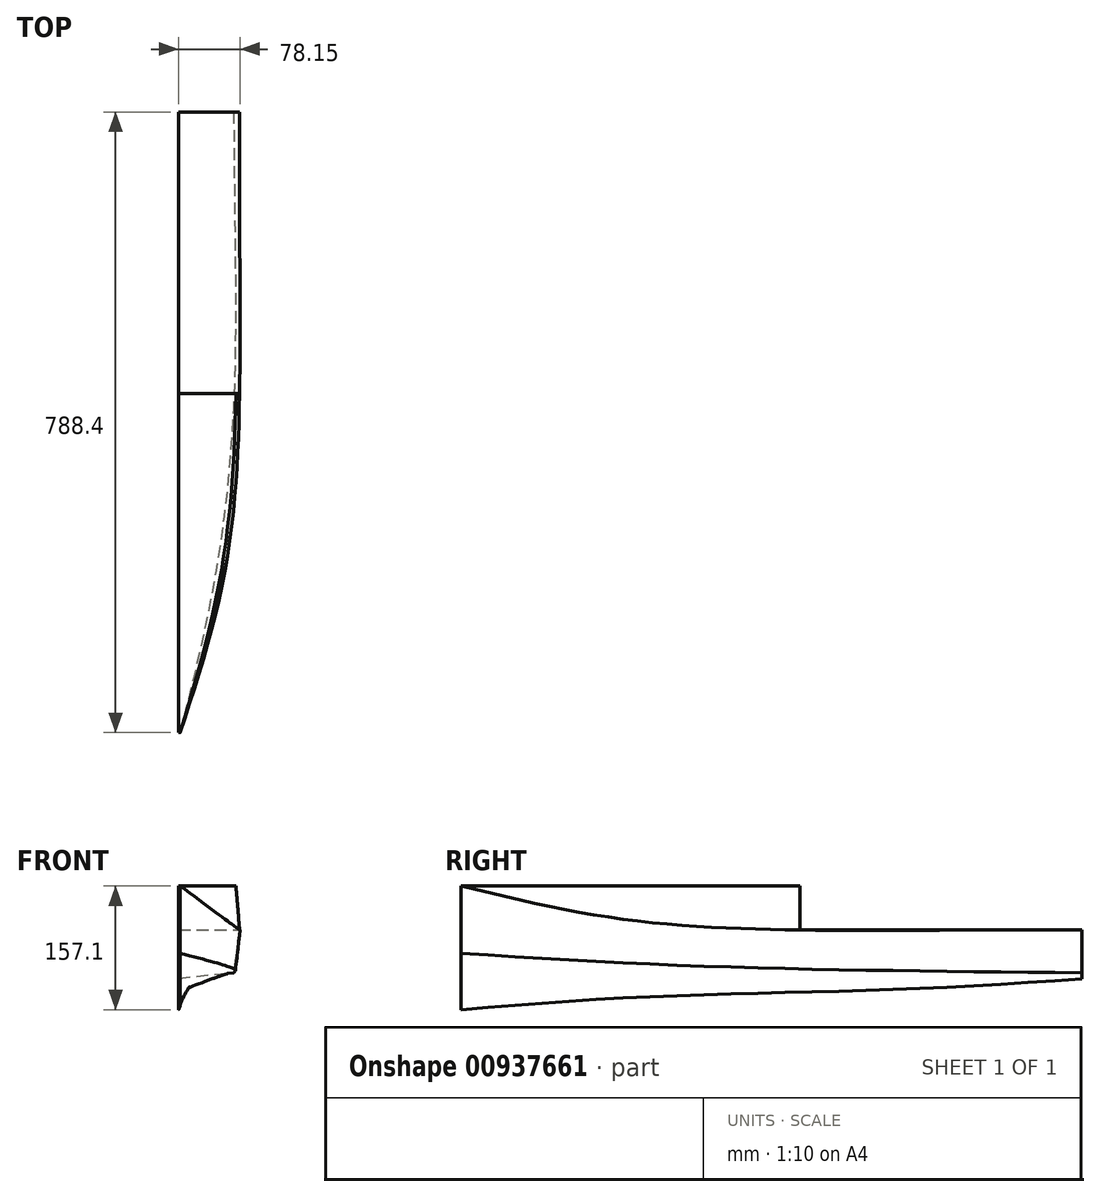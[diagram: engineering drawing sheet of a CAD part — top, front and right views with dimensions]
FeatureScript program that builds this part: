
annotation { "Feature Type Name" : "Feature", "Feature Type Description" : "" }
export const myFeature = defineFeature(function(context is Context, id is Id, definition is map)
    precondition{}
    {
        {
            var Q0;
            Q0=qCreatedBy(makeId("Front.planeOp"),FACE);
            var sketch = newSketch(context, id + "F0", { "sketchPlane" : qUnion([Q0])});
            skLineSegment(sketch, "E0", {"start": v(0, 0) * mm, "end": v(0, 43.5) * mm});
            skLineSegment(sketch, "E1", {"start": v(77.5, 43.5) * mm, "end": v(70, -11) * mm});
            skLineSegment(sketch, "E2", {"start": v(70, -11) * mm, "end": v(0, -18.5) * mm});
            skLineSegment(sketch, "E3", {"start": v(0, -18.5) * mm, "end": v(0, 0) * mm});
            skLineSegment(sketch, "E4", {"start": v(0, 43.5) * mm, "end": v(0, 99.4) * mm});
            skLineSegment(sketch, "E5", {"start": v(0, 99.4) * mm, "end": v(73, 99.4) * mm});
            skLineSegment(sketch, "E6", {"start": v(77.5, 43.5) * mm, "end": v(73, 99.4) * mm});
            skSolve(sketch);
        }
        {
            var Q0;
            Q0=qCreatedBy(makeId("Front.planeOp"),FACE);
            cPlane(context, id + "F1", {"entities" : qUnion([Q0]), "cplaneType" : CPlaneType.OFFSET, "offset" : 131.4 * mm, "width" : 150 * mm, "height" : 150 * mm});
        }
        {
            var Q0;
            Q0=qCreatedBy(id+"F1.planeOp",FACE);
            var sketch = newSketch(context, id + "F2", { "sketchPlane" : qUnion([Q0])});
            skLineSegment(sketch, "E7", {"start": v(0, 0) * mm, "end": v(0, 43.5) * mm});
            skLineSegment(sketch, "E8", {"start": v(77.5, 43.5) * mm, "end": v(71.3, -9.5) * mm});
            skLineSegment(sketch, "E9", {"start": v(71.3, -9.5) * mm, "end": v(0, -27.2) * mm});
            skLineSegment(sketch, "E10", {"start": v(0, -27.2) * mm, "end": v(0, 0) * mm});
            skLineSegment(sketch, "E11", {"start": v(0, 43.5) * mm, "end": v(0, 99.4) * mm});
            skLineSegment(sketch, "E12", {"start": v(0, 99.4) * mm, "end": v(73, 99.4) * mm});
            skLineSegment(sketch, "E13", {"start": v(77.5, 43.5) * mm, "end": v(73, 99.4) * mm});
            skSolve(sketch);
        }
        {
            var Q0;
            Q0=qCreatedBy(makeId("Front.planeOp"),FACE);
            cPlane(context, id + "F3", {"entities" : qUnion([Q0]), "cplaneType" : CPlaneType.OFFSET, "offset" : 358.1 * mm, "width" : 150 * mm, "height" : 150 * mm});
        }
        {
            var Q0;
            Q0=qCreatedBy(id+"F3.planeOp",FACE);
            var sketch = newSketch(context, id + "F4", { "sketchPlane" : qUnion([Q0])});
            skLineSegment(sketch, "E14", {"start": v(0, 0) * mm, "end": v(0, 43.5) * mm});
            skLineSegment(sketch, "E15", {"start": v(77.5, 43.5) * mm, "end": v(70.4, -5.9) * mm});
            skLineSegment(sketch, "E16", {"start": v(70.4, -5.9) * mm, "end": v(0, -35.5) * mm});
            skLineSegment(sketch, "E17", {"start": v(0, -35.5) * mm, "end": v(0, 0) * mm});
            skLineSegment(sketch, "E18", {"start": v(0, 43.5) * mm, "end": v(0, 99.4) * mm});
            skLineSegment(sketch, "E19", {"start": v(0, 99.4) * mm, "end": v(73, 99.4) * mm});
            skLineSegment(sketch, "E20", {"start": v(77.5, 43.5) * mm, "end": v(73, 99.4) * mm});
            skSolve(sketch);
        }
        {
            var Q0;
            Q0=qCreatedBy(makeId("Front.planeOp"),FACE);
            cPlane(context, id + "F5", {"entities" : qUnion([Q0]), "cplaneType" : CPlaneType.OFFSET, "offset" : 608.4 * mm, "width" : 150 * mm, "height" : 150 * mm});
        }
        {
            var Q0;
            Q0=qCreatedBy(id+"F5.planeOp",FACE);
            var sketch = newSketch(context, id + "F6", { "sketchPlane" : qUnion([Q0])});
            skLineSegment(sketch, "E21", {"start": v(0, 0) * mm, "end": v(0, 43.5) * mm});
            skLineSegment(sketch, "E22", {"start": v(43, 3.1) * mm, "end": v(0, -44.2) * mm});
            skLineSegment(sketch, "E23", {"start": v(0, -44.2) * mm, "end": v(0, 0) * mm});
            skLineSegment(sketch, "E24", {"start": v(49.7, 99.4) * mm, "end": v(0, 99.4) * mm});
            skLineSegment(sketch, "E25", {"start": v(0, 99.4) * mm, "end": v(0, 43.5) * mm});
            skLineSegment(sketch, "E26", {"start": v(54.03, 61) * mm, "end": v(49.7, 99.4) * mm});
            skLineSegment(sketch, "E27", {"start": v(54.03, 61) * mm, "end": v(43, 3.1) * mm});
            skSolve(sketch);
        }
        {
            var Q0;
            Q0=qCreatedBy(makeId("Front.planeOp"),FACE);
            cPlane(context, id + "F7", {"entities" : qUnion([Q0]), "cplaneType" : CPlaneType.OFFSET, "offset" : 788.4 * mm, "width" : 150 * mm, "height" : 150 * mm});
        }
        {
            var Q0;
            Q0=qCreatedBy(id+"F7.planeOp",FACE);
            var sketch = newSketch(context, id + "F8", { "sketchPlane" : qUnion([Q0])});
            skLineSegment(sketch, "E28", {"start": v(0, 0) * mm, "end": v(0, 43.5) * mm});
            skLineSegment(sketch, "E29", {"start": v(0, -57.7) * mm, "end": v(0, 0) * mm});
            skFitSpline(sketch, "E30", {"points": [v(2, 14) * mm, v(0, -57.7) * mm], "startDerivative": vector(0, -137.92) * mm, "endDerivative": vector(-7.5, 0) * mm});
            skLineSegment(sketch, "E31", {"start": v(2, 99.3) * mm, "end": v(2, 99.4) * mm});
            skLineSegment(sketch, "E32", {"start": v(2, 99.4) * mm, "end": v(0, 99.4) * mm});
            skLineSegment(sketch, "E33", {"start": v(0, 99.4) * mm, "end": v(0, 43.5) * mm});
            skLineSegment(sketch, "E34", {"start": v(2, 99.3) * mm, "end": v(2, 14) * mm});
            skSolve(sketch);
        }
        {
            var Q0;
            Q0=makeQuery(id+"F0.imprint","IMPRINT",FACE,{"disambiguationData":[TD([[makeQuery(id+"F0.imprint","IMPRINT",EDGE,{"derivedFrom":sQuery(id+"F0.wireOp",EDGE,"E1")}),-1.0]])]});
            var Q1;
            Q1=makeQuery(id+"F2.imprint","IMPRINT",FACE,{"disambiguationData":[TD([[makeQuery(id+"F2.imprint","IMPRINT",EDGE,{"derivedFrom":sQuery(id+"F2.wireOp",EDGE,"E8")}),-1.0]])]});
            var Q2;
            Q2=makeQuery(id+"F4.imprint","IMPRINT",FACE,{"disambiguationData":[TD([[makeQuery(id+"F4.imprint","IMPRINT",EDGE,{"derivedFrom":sQuery(id+"F4.wireOp",EDGE,"E15")}),-1.0]])]});
            var Q3;
            Q3=makeQuery(id+"F6.imprint","IMPRINT",FACE,{"disambiguationData":[TD([[makeQuery(id+"F6.imprint","IMPRINT",EDGE,{"derivedFrom":sQuery(id+"F6.wireOp",EDGE,"E22")}),-1.0]])]});
            var Q4;
            Q4=makeQuery(id+"F8.imprint","IMPRINT",FACE,{"disambiguationData":[TD([[makeQuery(id+"F8.imprint","IMPRINT",EDGE,{"derivedFrom":sQuery(id+"F8.wireOp",EDGE,"E29")}),-1.0]])]});
            loft(context, id + "F9", {"sheetProfilesArray" : [{ "sheetProfileEntities" : qUnion([Q0]) }, { "sheetProfileEntities" : qUnion([Q1]) }, { "sheetProfileEntities" : qUnion([Q2]) }, { "sheetProfileEntities" : qUnion([Q3]) }, { "sheetProfileEntities" : qUnion([Q4]) }]});
        }
        {
            var Q0;
            Q0=qCreatedBy(makeId("Right.planeOp"),FACE);
            cPlane(context, id + "F10", {"entities" : qUnion([Q0]), "cplaneType" : CPlaneType.OFFSET, "offset" : 80 * mm, "width" : 150 * mm, "height" : 150 * mm});
        }
        {
            var Q0;
            Q0=qCreatedBy(id+"F10.planeOp",FACE);
            var sketch = newSketch(context, id + "F11", { "sketchPlane" : qUnion([Q0])});
            skLineSegment(sketch, "E35.bottom", {"start": v(0, 43.5) * mm, "end": v(-358.1, 43.5) * mm});
            skLineSegment(sketch, "E35.top", {"start": v(0, 99.4) * mm, "end": v(-358.1, 99.4) * mm});
            skLineSegment(sketch, "E35.left", {"start": v(0, 43.5) * mm, "end": v(0, 99.4) * mm});
            skLineSegment(sketch, "E35.right", {"start": v(-358.1, 43.5) * mm, "end": v(-358.1, 99.4) * mm});
            skSolve(sketch);
        }
        {
            var Q0;
            Q0=makeQuery(id+"F11.imprint","IMPRINT",FACE,{"disambiguationData":[TD([[makeQuery(id+"F11.imprint","IMPRINT",EDGE,{"derivedFrom":sQuery(id+"F11.wireOp",EDGE,"E35.bottom")}),-1.0]])]});
            extrude(context, id + "F12", {"entities" : qUnion([Q0]), "operationType" : NewBodyOperationType.REMOVE, "oppositeDirection" : true, "depth" : 80 * mm, "offsetDistance" : 25 * mm});
        }
    });
